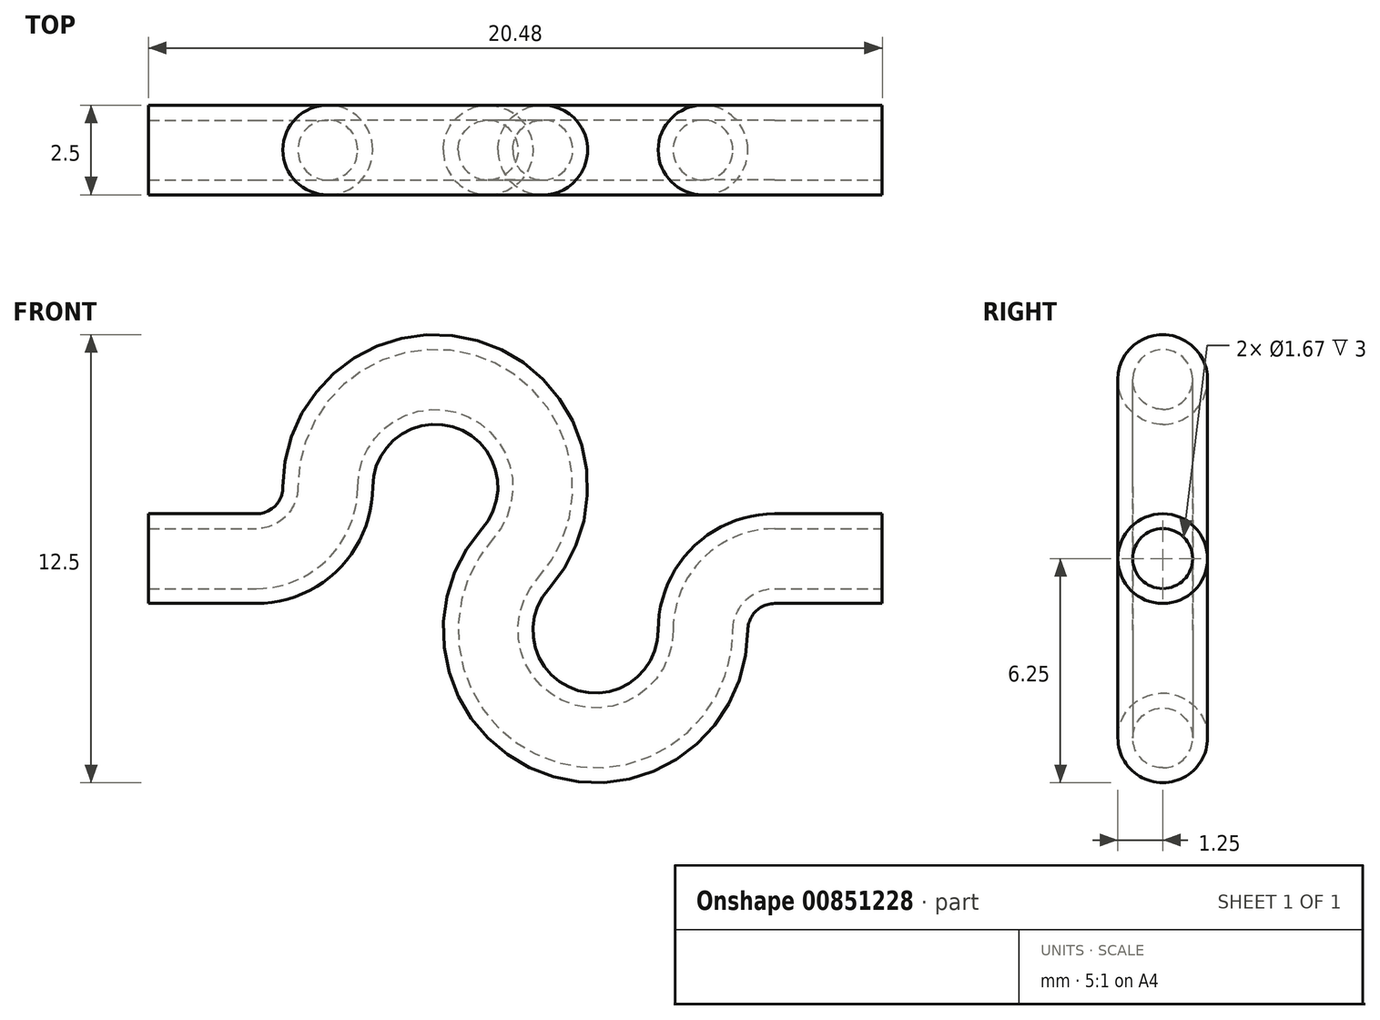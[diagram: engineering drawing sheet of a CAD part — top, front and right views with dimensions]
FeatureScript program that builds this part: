
annotation { "Feature Type Name" : "Feature", "Feature Type Description" : "" }
export const myFeature = defineFeature(function(context is Context, id is Id, definition is map)
    precondition{}
    {
        {
            var Q0;
            Q0=qCreatedBy(makeId("Front.planeOp"),FACE);
            var sketch = newSketch(context, id + "F0", { "sketchPlane" : qUnion([Q0])});
            skArc(sketch, "E0", {"start": v(0, 0) * mm, "mid": v(-1.17, 4.8) * mm, "end": v(-5.24, 2) * mm});
            skArc(sketch, "E1", {"start": v(0, 0) * mm, "mid": v(1.17, -4.8) * mm, "end": v(5.24, -2) * mm});
            skArc(sketch, "E2.filletArc", {"start": v(5.82, -0.86) * mm, "mid": v(5.81, -0.93) * mm, "end": v(5.81, -1) * mm});
            skLineSegment(sketch, "E3", {"start": v(-7.24, 0) * mm, "end": v(-10.24, 0) * mm});
            skArc(sketch, "E4", {"start": v(-7.24, 0) * mm, "mid": v(-5.82, 0.59) * mm, "end": v(-5.24, 2) * mm});
            skLineSegment(sketch, "E5.MirrorCS", {"start": v(7.24, 0) * mm, "end": v(10.24, 0) * mm});
            skArc(sketch, "E6.MirrorCS", {"start": v(7.24, 0) * mm, "mid": v(5.82, -0.59) * mm, "end": v(5.24, -2) * mm});
            skLineSegment(sketch, "E7", {"start": v(-5.24, 2) * mm, "end": v(10.61, 2) * mm, "construction": true});
            skLineSegment(sketch, "E8", {"start": v(2.24, -2) * mm, "end": v(16.92, -2) * mm, "construction": true});
            skSolve(sketch);
        }
        {
            var Q0;
            Q0=qCreatedBy(makeId("Right.planeOp"),FACE);
            var Q1;
            Q1=sQuery(id+"F0.wireOp",VERTEX,"E3.end");
            cPlane(context, id + "F1", {"entities" : qUnion([Q0, Q1]), "cplaneType" : CPlaneType.PLANE_POINT, "offset" : 25 * mm, "width" : 150 * mm, "height" : 150 * mm});
        }
        {
            var Q0;
            Q0=qCreatedBy(id+"F1.planeOp",FACE);
            var sketch = newSketch(context, id + "F2", { "sketchPlane" : qUnion([Q0])});
            skCircle(sketch, "E9", {"center": v(0, 0) * mm, "radius": 1.25 * mm});
            skCircle(sketch, "E10", {"center": v(0, 0) * mm, "radius": 0.84 * mm});
            skSolve(sketch);
        }
        {
            var Q0;
            Q0 = qSketchRegion(id + "F2", true);
            var Q1;
            Q1=sQuery(id+"F0.wireOp",EDGE,"E3");
            var Q2;
            Q2=sQuery(id+"F0.wireOp",EDGE,"E4");
            var Q3;
            Q3=sQuery(id+"F0.wireOp",EDGE,"E0");
            var Q4;
            Q4=sQuery(id+"F0.wireOp",EDGE,"E1");
            var Q5;
            Q5=sQuery(id+"F0.wireOp",EDGE,"E6.MirrorCS");
            var Q6;
            Q6=sQuery(id+"F0.wireOp",EDGE,"E5.MirrorCS");
            sweep(context, id + "F3", {"profiles" : qUnion([Q0]), "path" : qUnion([Q1, Q2, Q3, Q4, Q5, Q6])});
        }
    });
